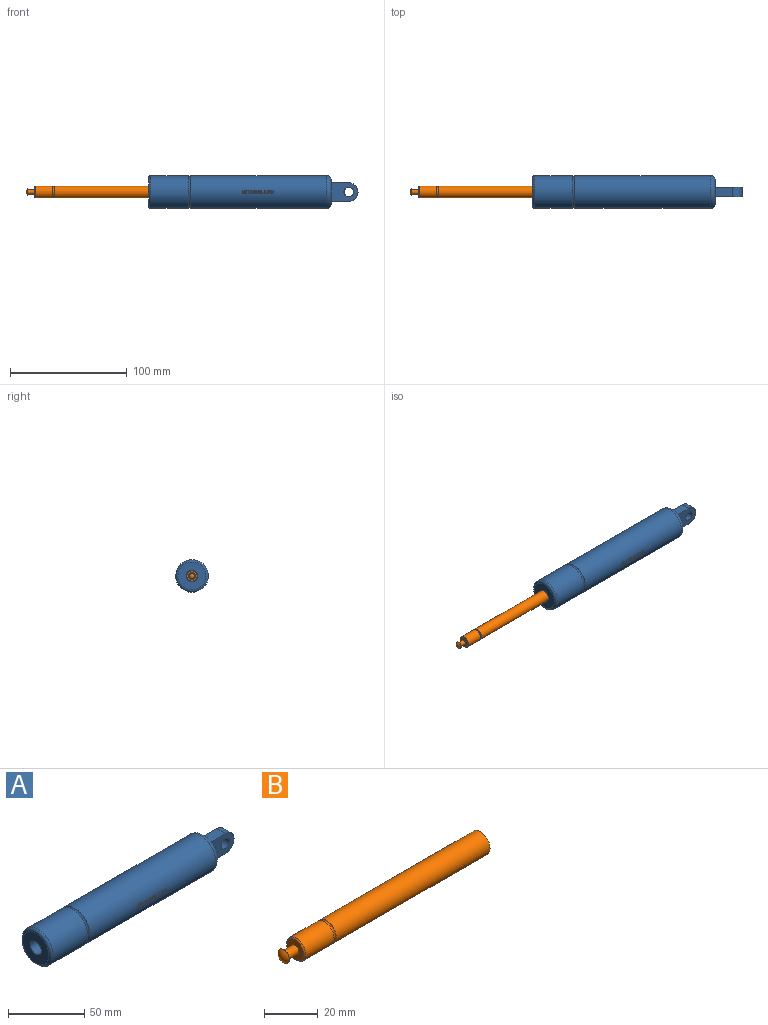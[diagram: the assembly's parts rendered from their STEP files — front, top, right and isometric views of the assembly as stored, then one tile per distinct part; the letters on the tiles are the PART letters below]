
ASSEMBLY  parts=2 mates=1
PART A: 113 faces, bbox 179.5x31.8x31.8 mm
  f0: torus R=14mm, axis (1,0,0), area 263.8mm2, adj f2,f5
  f1: torus R=10mm, axis (1,0,0), area 495.3mm2, adj f5,f109
  f2: cylinder r=14mm len=32mm, axis (-1,0,0), area 2814.9mm2, adj f0,f3
  f3: torus R=12mm, axis (1,0,0), area 262mm2, adj f2,f110
  f4: cylinder r=4.01mm len=8.02mm, axis (0,1,0), area 201.4mm2, adj f107,f108
  f5: cylinder r=14mm len=116.5mm, axis (-1,0,0), area 10208.9mm2, adj f0,f1,f6,f7,f8,f9,f10,f11
  f6: plane 0.67x0.22mm, normal (0,0,-1), area 0.2mm2, adj f5,f7,f17,f18
  f7: plane 1.94x0.28mm, normal (-1,0,0), area 0.5mm2, adj f5,f6,f8,f18
  f8: cylinder r=0.56mm len=0.56mm, axis (0,1,0), area 0.2mm2, adj f5,f7,f9,f18
  f9: plane 2.36x0.22mm, normal (0,0,1), area 0.5mm2, adj f5,f8,f10,f18
  f10: cylinder r=0.56mm len=0.56mm, axis (0,1,0), area 0.2mm2, adj f5,f9,f11,f18
  f11: plane 1.94x0.28mm, normal (1,0,0), area 0.5mm2, adj f5,f10,f12,f18
  f12: plane 0.67x0.22mm, normal (0,0,-1), area 0.2mm2, adj f5,f11,f13,f18
  f13: plane 1.73x0.28mm, normal (-1,0,0), area 0.5mm2, adj f5,f12,f14,f18
  f14: cylinder r=0.22mm len=0.27mm, axis (0,1,0), area 0.1mm2, adj f5,f13,f15,f18
  f15: plane 1.69x0.26mm, normal (0,0,-1), area 0.4mm2, adj f5,f14,f16,f18
  f16: cylinder r=0.22mm len=0.27mm, axis (0,1,0), area 0.1mm2, adj f5,f15,f17,f18
  f17: plane 1.73x0.28mm, normal (1,0,0), area 0.5mm2, adj f5,f6,f16,f18
  f18: plane 3.48x2.5mm, normal (0,-1,0), area 4.4mm2, adj f6,f7,f8,f9,f10,f11,f12,f13
  f19: plane 2.5x0.28mm, normal (-1,0,0), area 0.7mm2, adj f5,f20,f22,f23
  f20: plane 0.67x0.22mm, normal (0,0,1), area 0.2mm2, adj f5,f19,f21,f23
  f21: plane 2.5x0.28mm, normal (1,0,0), area 0.7mm2, adj f5,f20,f22,f23
  f22: plane 0.67x0.22mm, normal (0,0,-1), area 0.2mm2, adj f5,f19,f21,f23
  f23: plane 2.5x0.67mm, normal (0,-1,0), area 1.7mm2, adj f19,f20,f21,f22
  f24: plane 0.9x0.44mm, normal (0.9,0,0.43), area 0.3mm2, adj f25,f31,f36,f103
  f25: plane 0.9x0.26mm, normal (0,0,1), area 0.2mm2, adj f24,f30,f36,f103
  f26: plane 1.9x0.26mm, normal (0,0,1), area 0.5mm2, adj f5,f27,f35,f36
  f27: plane 0.48x0.26mm, normal (-0.9,0,0.43), area 0.1mm2, adj f5,f26,f28,f36
  f28: plane 0.83x0.22mm, normal (0,0,1), area 0.2mm2, adj f5,f27,f29,f36
  f29: plane 2.51x1.21mm, normal (0.9,0,-0.43), area 0.7mm2, adj f5,f28,f32,f36
  f30: plane 0.9x0.44mm, normal (-0.9,0,0.43), area 0.3mm2, adj f25,f31,f36,f103
  f31: plane 1.77x0.28mm, normal (0,0,-1), area 0.5mm2, adj f24,f30,f36,f103
  f32: plane 1.61x0.22mm, normal (0,0,-1), area 0.4mm2, adj f5,f29,f33,f36
  f33: plane 2.51x1.21mm, normal (-0.9,0,-0.43), area 0.7mm2, adj f5,f32,f34,f36
  f34: plane 0.83x0.22mm, normal (0,0,1), area 0.2mm2, adj f5,f33,f35,f36
  f35: plane 0.48x0.26mm, normal (0.9,0,0.44), area 0.1mm2, adj f5,f26,f34,f36
  f36: plane 4.02x2.51mm, normal (0,-1,0), area 4.8mm2, adj f24,f25,f26,f27,f28,f29,f30,f31
  f37: plane 2.66x0.26mm, normal (0,0,1), area 0.7mm2, adj f5,f38,f48,f49
  f38: cylinder r=0.22mm len=0.43mm, axis (0,1,0), area 0.2mm2, adj f5,f37,f39,f49
  f39: plane 1.96x0.28mm, normal (0,0,-1), area 0.5mm2, adj f5,f38,f40,f49
  f40: cylinder r=0.76mm len=1.53mm, axis (0,1,0), area 0.6mm2, adj f5,f39,f41,f49
  f41: plane 2.8x0.22mm, normal (0,0,1), area 0.6mm2, adj f5,f40,f42,f49
  f42: plane 0.55x0.26mm, normal (1,0,0), area 0.1mm2, adj f5,f41,f43,f49
  f43: plane 2.66x0.26mm, normal (0,0,-1), area 0.7mm2, adj f5,f42,f44,f49
  f44: cylinder r=0.22mm len=0.43mm, axis (0,1,0), area 0.2mm2, adj f5,f43,f45,f49
  f45: plane 1.96x0.28mm, normal (0,0,1), area 0.5mm2, adj f5,f44,f46,f49
  f46: cylinder r=0.76mm len=1.53mm, axis (0,1,0), area 0.6mm2, adj f5,f45,f47,f49
  f47: plane 2.8x0.22mm, normal (0,0,-1), area 0.6mm2, adj f5,f46,f48,f49
  f48: plane 0.55x0.26mm, normal (-1,0,0), area 0.1mm2, adj f5,f37,f47,f49
  f49: plane 3.63x2.51mm, normal (0,-1,0), area 6mm2, adj f37,f38,f39,f40,f41,f42,f43,f44
  f50: plane 0.67x0.22mm, normal (0,0,1), area 0.2mm2, adj f5,f51,f57,f58
  f51: plane 1.95x0.28mm, normal (1,0,0), area 0.5mm2, adj f5,f50,f52,f58
  f52: plane 1.43x0.26mm, normal (0,0,1), area 0.4mm2, adj f5,f51,f53,f58
  f53: plane 0.55x0.26mm, normal (1,0,0), area 0.1mm2, adj f5,f52,f54,f58
  f54: plane 3.57x0.22mm, normal (0,0,-1), area 0.8mm2, adj f5,f53,f55,f58
  f55: plane 0.55x0.26mm, normal (-1,0,0), area 0.1mm2, adj f5,f54,f56,f58
  f56: plane 1.47x0.26mm, normal (0,0,1), area 0.4mm2, adj f5,f55,f57,f58
  f57: plane 1.95x0.28mm, normal (-1,0,0), area 0.5mm2, adj f5,f50,f56,f58
  f58: plane 3.57x2.5mm, normal (0,-1,0), area 3.3mm2, adj f50,f51,f52,f53,f54,f55,f56,f57
  f59: plane 1.99x0.28mm, normal (0,0,-1), area 0.6mm2, adj f60,f71,f80,f102
  f60: cylinder r=0.21mm len=0.41mm, axis (0,1,0), area 0.2mm2, adj f59,f70,f80,f102
  f61: cylinder r=0.21mm len=0.41mm, axis (0,1,0), area 0.2mm2, adj f62,f73,f80,f101
  f62: plane 1.99x0.28mm, normal (0,0,1), area 0.6mm2, adj f61,f72,f80,f101
  f63: cylinder r=0.28mm len=0.28mm, axis (0,1,0), area 0mm2, adj f5,f64,f79,f80
  f64: cylinder r=0.28mm len=0.28mm, axis (0,1,0), area 0mm2, adj f5,f63,f65,f80
  f65: cylinder r=0.7mm len=0.28mm, axis (0,1,0), area 0.1mm2, adj f5,f64,f66,f80
  f66: cylinder r=0.87mm len=0.46mm, axis (0,1,0), area 0.1mm2, adj f5,f65,f67,f80
  f67: cylinder r=0.58mm len=0.48mm, axis (0,1,0), area 0.2mm2, adj f5,f66,f68,f80
  f68: cylinder r=1.03mm len=0.27mm, axis (0,1,0), area 0.1mm2, adj f5,f67,f69,f80
  f69: plane 2.8x0.22mm, normal (0,0,1), area 0.6mm2, adj f5,f68,f74,f80
  f70: plane 1.99x0.26mm, normal (0,0,1), area 0.5mm2, adj f60,f71,f80,f102
  f71: plane 0.41x0.28mm, normal (-1,0,0), area 0.1mm2, adj f59,f70,f80,f102
  f72: plane 0.41x0.28mm, normal (-1,0,0), area 0.1mm2, adj f62,f73,f80,f101
  f73: plane 1.99x0.26mm, normal (0,0,-1), area 0.5mm2, adj f61,f72,f80,f101
  f74: plane 2.5x0.28mm, normal (1,0,0), area 0.7mm2, adj f5,f69,f75,f80
  f75: plane 2.8x0.22mm, normal (0,0,-1), area 0.6mm2, adj f5,f74,f76,f80
  f76: cylinder r=1.03mm len=0.27mm, axis (0,1,0), area 0.1mm2, adj f5,f75,f77,f80
  f77: cylinder r=0.58mm len=0.48mm, axis (0,1,0), area 0.2mm2, adj f5,f76,f78,f80
  f78: cylinder r=0.87mm len=0.46mm, axis (0,1,0), area 0.1mm2, adj f5,f77,f79,f80
  f79: cylinder r=0.7mm len=0.28mm, axis (0,1,0), area 0.1mm2, adj f5,f63,f78,f80
  f80: plane 3.55x2.5mm, normal (0,-1,0), area 6.8mm2, adj f59,f60,f61,f62,f63,f64,f65,f66
  f81: plane 2.23x0.26mm, normal (0,0,-1), area 0.6mm2, adj f5,f82,f86,f87
  f82: plane 0.55x0.26mm, normal (-1,0,0), area 0.1mm2, adj f5,f81,f83,f87
  f83: plane 2.9x0.22mm, normal (0,0,1), area 0.6mm2, adj f5,f82,f84,f87
  f84: plane 2.5x0.28mm, normal (1,0,0), area 0.7mm2, adj f5,f83,f85,f87
  f85: plane 0.67x0.22mm, normal (0,0,-1), area 0.2mm2, adj f5,f84,f86,f87
  f86: plane 1.96x0.28mm, normal (-1,0,0), area 0.5mm2, adj f5,f81,f85,f87
  f87: plane 2.9x2.5mm, normal (0,-1,0), area 2.9mm2, adj f81,f82,f83,f84,f85,f86
  f88: plane 2.66x0.26mm, normal (0,0,1), area 0.7mm2, adj f5,f89,f99,f100
  f89: cylinder r=0.22mm len=0.43mm, axis (0,1,0), area 0.2mm2, adj f5,f88,f90,f100
  f90: plane 1.97x0.28mm, normal (0,0,-1), area 0.5mm2, adj f5,f89,f91,f100
  f91: cylinder r=0.76mm len=1.53mm, axis (0,1,0), area 0.6mm2, adj f5,f90,f92,f100
  f92: plane 2.81x0.22mm, normal (0,0,1), area 0.6mm2, adj f5,f91,f93,f100
  f93: plane 0.55x0.26mm, normal (1,0,0), area 0.1mm2, adj f5,f92,f94,f100
  f94: plane 2.66x0.26mm, normal (0,0,-1), area 0.7mm2, adj f5,f93,f95,f100
  f95: cylinder r=0.22mm len=0.43mm, axis (0,1,0), area 0.2mm2, adj f5,f94,f96,f100
  f96: plane 1.97x0.28mm, normal (0,0,1), area 0.5mm2, adj f5,f95,f97,f100
  f97: cylinder r=0.76mm len=1.53mm, axis (0,1,0), area 0.6mm2, adj f5,f96,f98,f100
  f98: plane 2.81x0.22mm, normal (0,0,-1), area 0.6mm2, adj f5,f97,f99,f100
  f99: plane 0.55x0.26mm, normal (-1,0,0), area 0.1mm2, adj f5,f88,f98,f100
  f100: plane 3.64x2.51mm, normal (0,-1,0), area 6mm2, adj f88,f89,f90,f91,f92,f93,f94,f95
  f101: cylinder r=14mm len=1.99mm, axis (-1,0,0), area 0.8mm2, adj f61,f62,f72,f73
  f102: cylinder r=14mm len=1.99mm, axis (-1,0,0), area 0.8mm2, adj f59,f60,f70,f71
  f103: cylinder r=14mm len=1.77mm, axis (-1,0,0), area 1.2mm2, adj f24,f25,f30,f31
  f104: plane 15x8mm, normal (0,0,1), area 120mm2, adj f105,f107,f108,f109
  f105: cylinder r=8mm len=16mm, axis (0,1,0), area 201.1mm2, adj f104,f106,f107,f108
  f106: plane 15x8mm, normal (0,0,-1), area 120mm2, adj f105,f107,f108,f109
  f107: plane 23x16mm, normal (0,1,0), area 290.1mm2, adj f4,f104,f105,f106,f109
  f108: plane 23x16mm, normal (0,-1,0), area 290.1mm2, adj f4,f104,f105,f106,f109
  f109: plane 20x20mm, normal (1,0,0), area 186.2mm2, adj f1,f104,f106,f107,f108
  f110: plane 24x24mm, normal (-1,0,0), area 373.8mm2, adj f3,f111
  f111: cylinder r=5mm len=100mm, axis (-1,0,0), area 3141.6mm2, adj f110,f112
  f112: plane 10x10mm, normal (-1,0,0), area 78.5mm2, adj f111
PART B: 9 faces, bbox 105x11.7x11.7 mm
  f0: torus R=5mm, axis (1,0,0), area 50.9mm2, adj f1,f5
  f1: cylinder r=5mm len=14.89mm, axis (1,0,0), area 467.8mm2, adj f0,f2
  f2: cone r=4.72mm half-angle=45deg, axis (1,0,0), area 23.3mm2, adj f1,f7
  f3: sphere r=3.75mm, area 35.3mm2, adj f6
  f4: cylinder r=2mm len=6mm, axis (1,0,0), area 75.4mm2, adj f6,f7
  f5: cylinder r=5mm len=80.95mm, axis (1,0,0), area 2543mm2, adj f0,f8
  f6: plane 6x6mm, normal (1,0,0), area 15.7mm2, adj f3,f4
  f7: plane 8.89x8.89mm, normal (-1,0,0), area 49.5mm2, adj f2,f4
  f8: plane 10x10mm, normal (1,0,0), area 78.5mm2, adj f5
PLACE A t=(-20.58,-11.2,5.15)mm
PLACE B t=(-20.58,-11.2,5.15)mm
MATE slider B.f0 <-> A.f0  axis (1,0,0) through (-20.58,-11.2,5.15)mm
